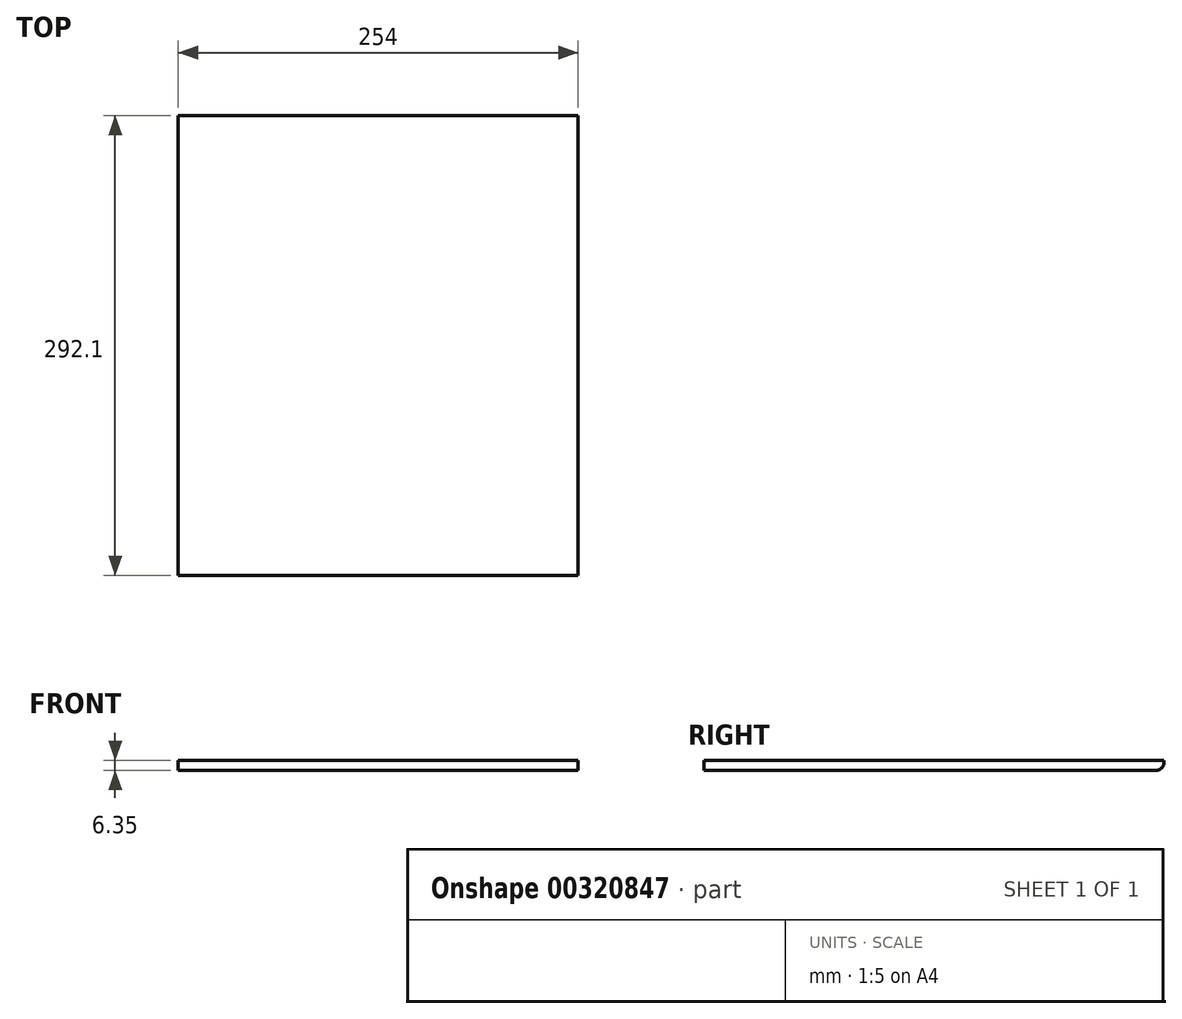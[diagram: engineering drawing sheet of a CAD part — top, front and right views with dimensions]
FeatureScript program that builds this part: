
annotation { "Feature Type Name" : "Feature", "Feature Type Description" : "" }
export const myFeature = defineFeature(function(context is Context, id is Id, definition is map)
    precondition{}
    {
        {
            var Q0;
            Q0=qCreatedBy(makeId("Top.planeOp"),FACE);
            var sketch = newSketch(context, id + "F0", { "sketchPlane" : qUnion([Q0])});
            skLineSegment(sketch, "E0.bottom", {"start": v(127, 146.05) * mm, "end": v(-127, 146.05) * mm});
            skLineSegment(sketch, "E0.top", {"start": v(127, -146.05) * mm, "end": v(-127, -146.05) * mm});
            skLineSegment(sketch, "E0.left", {"start": v(127, 146.05) * mm, "end": v(127, -146.05) * mm});
            skLineSegment(sketch, "E0.right", {"start": v(-127, 146.05) * mm, "end": v(-127, -146.05) * mm});
            skPoint(sketch, "E0.middle", {"position": v(0, 0) * mm});
            skSolve(sketch);
        }
        {
            var Q0;
            Q0=makeQuery(id+"F0.imprint","IMPRINT",FACE,{"disambiguationData":[TD([[makeQuery(id+"F0.imprint","IMPRINT",EDGE,{"derivedFrom":sQuery(id+"F0.wireOp",EDGE,"E0.bottom")}),1.0]])]});
            extrude(context, id + "F1", {"entities" : qUnion([Q0]), "depth" : 6.35 * mm});
        }
        {
            var Q0;
            Q0=makeQuery(id+"F1.opExtrude","CAP_EDGE",EDGE,{"disambiguationData":[OSD([sQuery(id+"F0.wireOp",EDGE,"E0.bottom")])],"isStart":true});
            fillet(context, id + "F2", {"entities" : qUnion([Q0]), "radius" : 5.08 * mm, "tangentPropagation" : true, "allowEdgeOverflow" : false});
        }
    });
